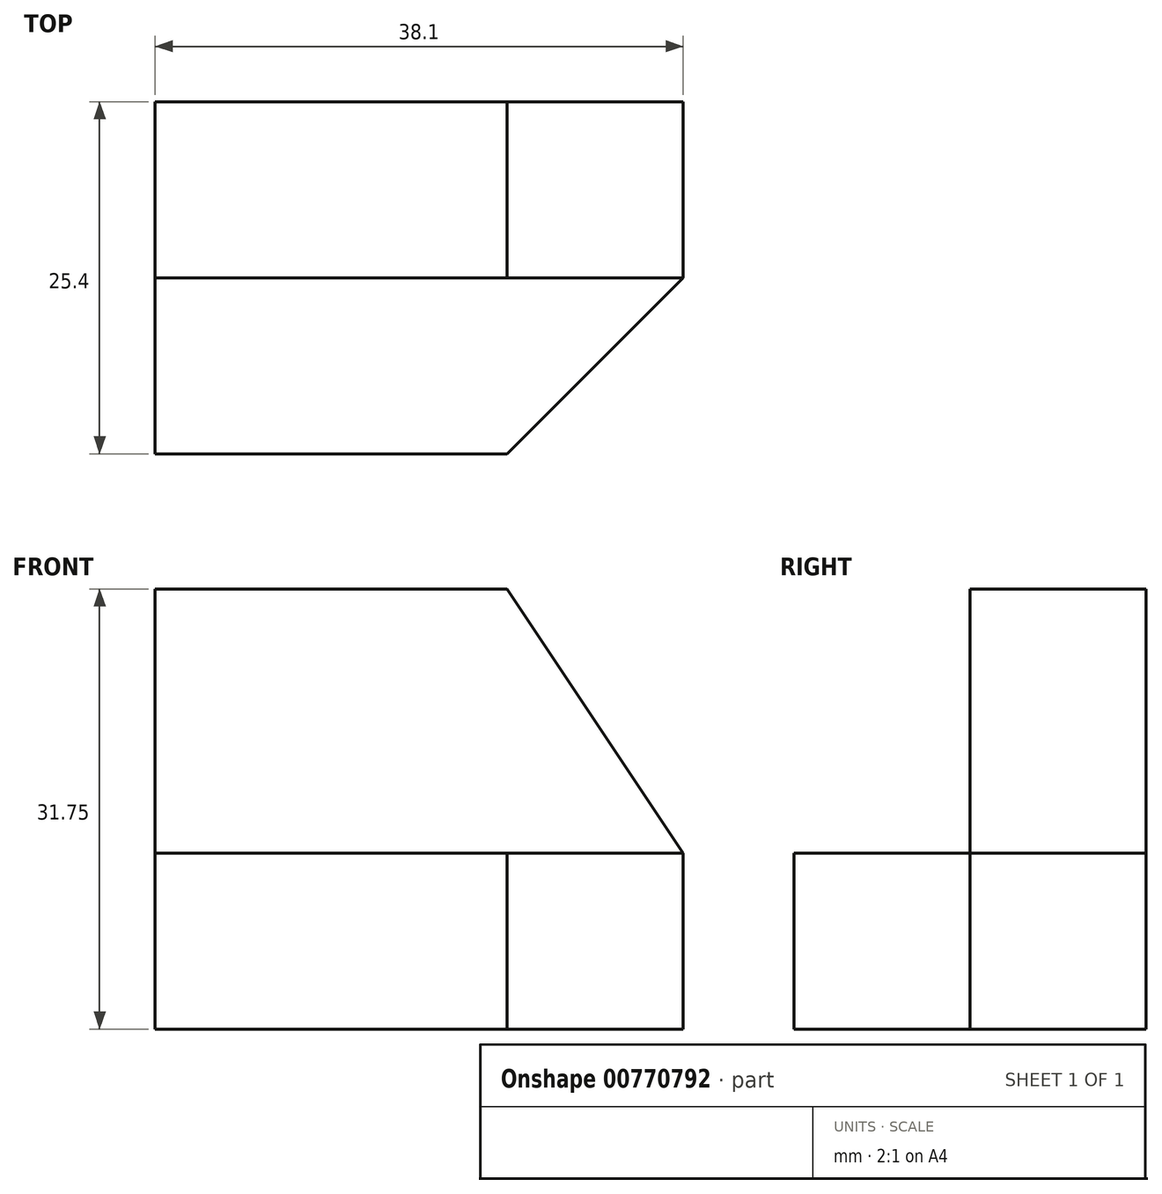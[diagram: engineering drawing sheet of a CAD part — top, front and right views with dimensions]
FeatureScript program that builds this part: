
annotation { "Feature Type Name" : "Feature", "Feature Type Description" : "" }
export const myFeature = defineFeature(function(context is Context, id is Id, definition is map)
    precondition{}
    {
        {
            var Q0;
            Q0=qCreatedBy(makeId("Front.planeOp"),FACE);
            var sketch = newSketch(context, id + "F0", { "sketchPlane" : qUnion([Q0])});
            skLineSegment(sketch, "E0", {"start": v(0, 0) * mm, "end": v(38.1, 0) * mm});
            skLineSegment(sketch, "E1", {"start": v(38.1, 0) * mm, "end": v(38.1, 31.75) * mm});
            skLineSegment(sketch, "E2", {"start": v(38.1, 31.75) * mm, "end": v(0, 31.75) * mm});
            skLineSegment(sketch, "E3", {"start": v(0, 31.75) * mm, "end": v(0, 0) * mm});
            skSolve(sketch);
        }
        {
            var Q0;
            Q0=makeQuery(id+"F0.imprint","IMPRINT",FACE,{"disambiguationData":[TD([[makeQuery(id+"F0.imprint","IMPRINT",EDGE,{"derivedFrom":sQuery(id+"F0.wireOp",EDGE,"E0")}),1.0]])]});
            extrude(context, id + "F1", {"entities" : qUnion([Q0]), "depth" : 25.4 * mm, "offsetDistance" : 25.4 * mm});
        }
        {
            var Q0;
            Q0=makeQuery(id+"F1.opExtrude","CAP_FACE",FACE,{"disambiguationData":[OSD([sQuery(id+"F0.wireOp",EDGE,"E0"),sQuery(id+"F0.wireOp",EDGE,"E1"),sQuery(id+"F0.wireOp",EDGE,"E2"),sQuery(id+"F0.wireOp",EDGE,"E3")])],"isStart":false});
            var sketch = newSketch(context, id + "F2", { "sketchPlane" : qUnion([Q0])});
            skLineSegment(sketch, "E4", {"start": v(0, 12.7) * mm, "end": v(38.1, 12.7) * mm});
            skLineSegment(sketch, "E5", {"start": v(38.1, 12.7) * mm, "end": v(38.1, 31.75) * mm});
            skLineSegment(sketch, "E6", {"start": v(38.1, 31.75) * mm, "end": v(0, 31.75) * mm});
            skLineSegment(sketch, "E7", {"start": v(0, 31.75) * mm, "end": v(0, 12.7) * mm});
            skSolve(sketch);
        }
        {
            var Q0;
            Q0=makeQuery(id+"F2.imprint","IMPRINT",FACE,{"disambiguationData":[TD([[makeQuery(id+"F2.imprint","IMPRINT",EDGE,{"derivedFrom":sQuery(id+"F2.wireOp",EDGE,"E4")}),1.0]])]});
            extrude(context, id + "F3", {"entities" : qUnion([Q0]), "operationType" : NewBodyOperationType.REMOVE, "oppositeDirection" : true, "depth" : 12.7 * mm, "offsetDistance" : 25.4 * mm});
        }
        {
            var Q0;
            Q0=makeQuery(id+"F3.boolean.opBoolean","COPY",FACE,{"derivedFrom":makeQuery(id+"F3.opExtrude","CAP_FACE",FACE,{"disambiguationData":[OSD([sQuery(id+"F2.wireOp",EDGE,"E4"),sQuery(id+"F2.wireOp",EDGE,"E5"),sQuery(id+"F2.wireOp",EDGE,"E6"),sQuery(id+"F2.wireOp",EDGE,"E7")])],"isStart":false})});
            var sketch = newSketch(context, id + "F4", { "sketchPlane" : qUnion([Q0])});
            skLineSegment(sketch, "E8", {"start": v(38.1, 31.75) * mm, "end": v(25.4, 31.75) * mm});
            skLineSegment(sketch, "E9", {"start": v(25.4, 31.75) * mm, "end": v(38.1, 12.7) * mm});
            skLineSegment(sketch, "E10", {"start": v(38.1, 12.7) * mm, "end": v(38.1, 31.75) * mm});
            skSolve(sketch);
        }
        {
            var Q0;
            Q0=makeQuery(id+"F4.imprint","IMPRINT",FACE,{"disambiguationData":[TD([[makeQuery(id+"F4.imprint","IMPRINT",EDGE,{"derivedFrom":sQuery(id+"F4.wireOp",EDGE,"E8")}),1.0]])]});
            extrude(context, id + "F5", {"entities" : qUnion([Q0]), "operationType" : NewBodyOperationType.REMOVE, "oppositeDirection" : true, "depth" : 12.7 * mm, "offsetDistance" : 25.4 * mm});
        }
        {
            var Q0;
            Q0=makeQuery(id+"F3.boolean.opBoolean","COPY",FACE,{"derivedFrom":makeQuery(id+"F3.opExtrude","SWEPT_FACE",FACE,{"disambiguationData":[OSD([sQuery(id+"F2.wireOp",EDGE,"E4")])]})});
            var sketch = newSketch(context, id + "F6", { "sketchPlane" : qUnion([Q0])});
            skLineSegment(sketch, "E11", {"start": v(38.1, -12.7) * mm, "end": v(38.1, -25.4) * mm});
            skLineSegment(sketch, "E12", {"start": v(38.1, -25.4) * mm, "end": v(25.4, -25.4) * mm});
            skLineSegment(sketch, "E13", {"start": v(25.4, -25.4) * mm, "end": v(38.1, -12.7) * mm});
            skSolve(sketch);
        }
        {
            var Q0;
            Q0=makeQuery(id+"F6.imprint","IMPRINT",FACE,{"disambiguationData":[TD([[makeQuery(id+"F6.imprint","IMPRINT",EDGE,{"derivedFrom":sQuery(id+"F6.wireOp",EDGE,"E11")}),-1.0]])]});
            extrude(context, id + "F7", {"entities" : qUnion([Q0]), "operationType" : NewBodyOperationType.REMOVE, "oppositeDirection" : true, "depth" : 12.7 * mm, "offsetDistance" : 25.4 * mm});
        }
    });
